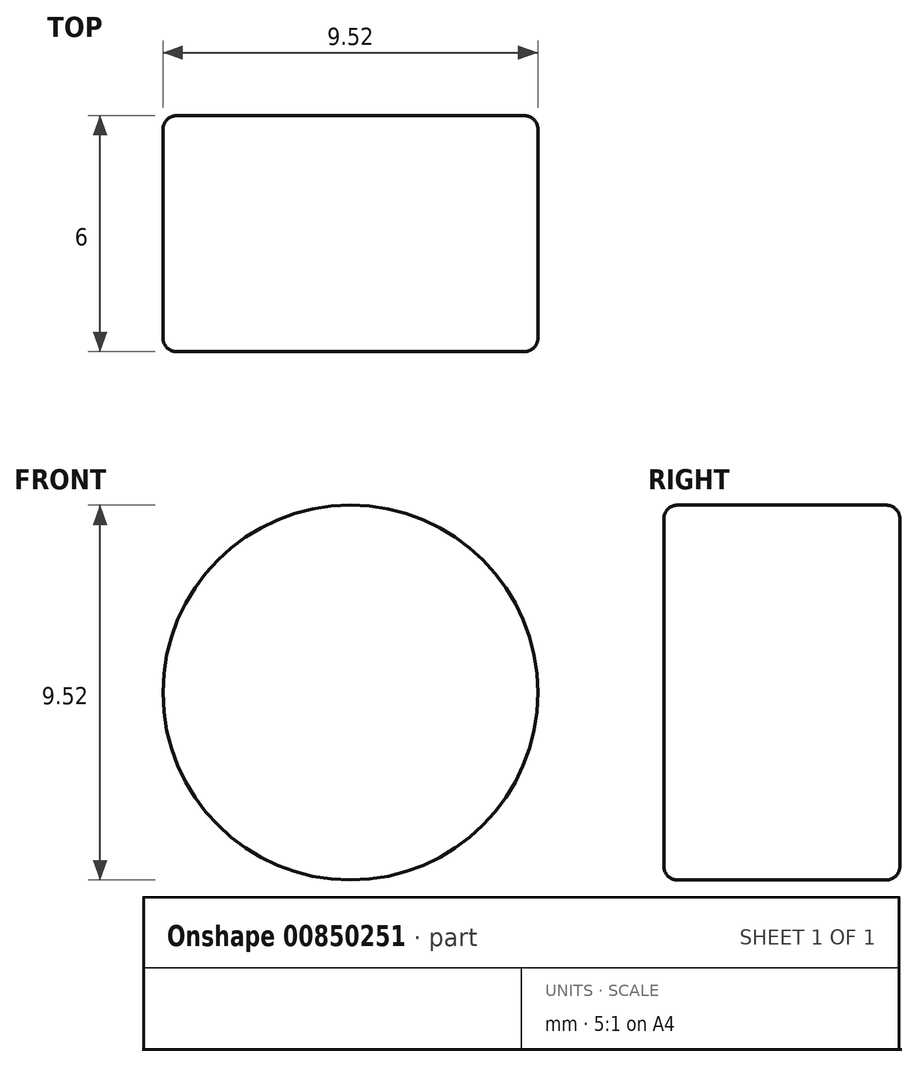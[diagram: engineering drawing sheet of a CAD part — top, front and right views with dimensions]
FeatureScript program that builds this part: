
annotation { "Feature Type Name" : "Feature", "Feature Type Description" : "" }
export const myFeature = defineFeature(function(context is Context, id is Id, definition is map)
    precondition{}
    {
        {
            var Q0;
            Q0=qCreatedBy(makeId("Front.planeOp"),FACE);
            var sketch = newSketch(context, id + "F0", { "sketchPlane" : qUnion([Q0])});
            skCircle(sketch, "E0", {"center": v(0, 0) * mm, "radius": 4.76 * mm});
            skSolve(sketch);
        }
        {
            var Q0;
            Q0 = qSketchRegion(id + "F0", true);
            extrude(context, id + "F1", {"entities" : qUnion([Q0]), "endBound" : BoundingType.SYMMETRIC, "depth" : 3 * mm, "offsetDistance" : 25 * mm});
        }
        {
            var Q0;
            Q0=makeQuery(id+"F1.opExtrude","CAP_FACE",FACE,{"disambiguationData":[OSD([sQuery(id+"F0.wireOp",EDGE,"E0")])],"isStart":false});
            var sketch = newSketch(context, id + "F2", { "sketchPlane" : qUnion([Q0])});
            skCircle(sketch, "E1", {"center": v(0, 0) * mm, "radius": 4.76 * mm});
            skSolve(sketch);
        }
        {
            var Q0;
            Q0 = qSketchRegion(id + "F2", true);
            extrude(context, id + "F3", {"entities" : qUnion([Q0]), "operationType" : NewBodyOperationType.ADD, "depth" : 1.5 * mm, "offsetDistance" : 25 * mm});
        }
        {
            var Q0;
            Q0=makeQuery(id+"F3.opExtrude","CAP_EDGE",EDGE,{"disambiguationData":[OSD([sQuery(id+"F2.wireOp",EDGE,"E1")])],"isStart":false});
            fillet(context, id + "F4", {"entities" : qUnion([Q0]), "radius" : 0.35 * mm, "tangentPropagation" : true, "allowEdgeOverflow" : false});
        }
        {
            var Q0;
            Q0=makeQuery(id+"F1.opExtrude","SWEPT_BODY",BODY,{"disambiguationData":[OSD([sQuery(id+"F0.wireOp",EDGE,"E0")])]});
            var Q1;
            Q1=qCreatedBy(makeId("Front.planeOp"),FACE);
            mirror(context, id + "F5", {"operationType" : NewBodyOperationType.ADD, "entities" : qUnion([Q0]), "mirrorPlane" : qUnion([Q1])});
        }
    });
